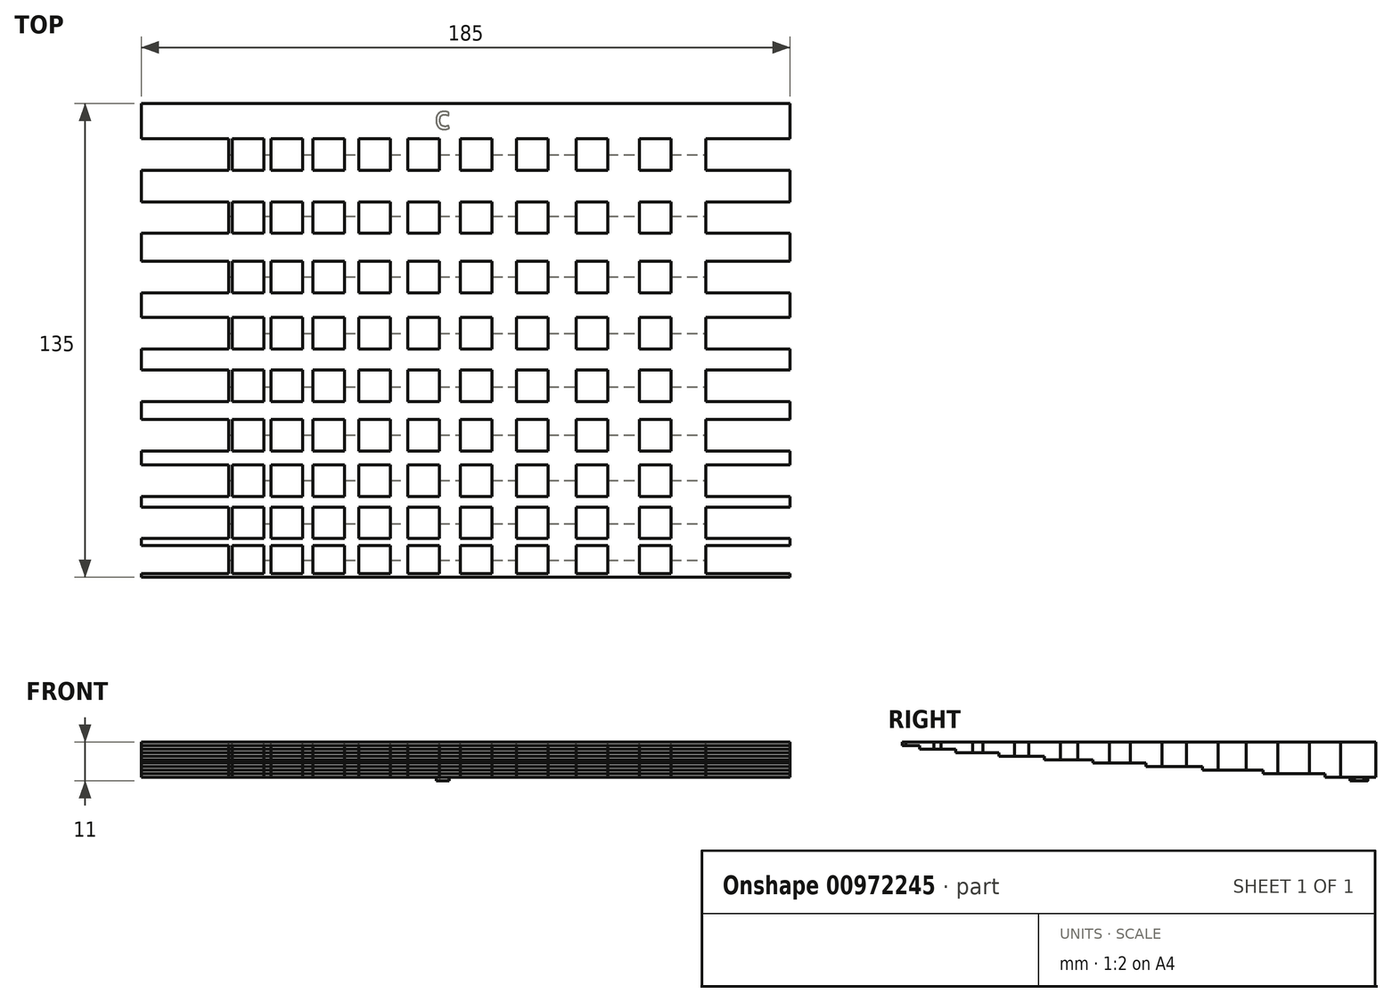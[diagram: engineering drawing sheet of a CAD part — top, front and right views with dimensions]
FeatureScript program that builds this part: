
annotation { "Feature Type Name" : "Feature", "Feature Type Description" : "" }
export const myFeature = defineFeature(function(context is Context, id is Id, definition is map)
    precondition{}
    {
        {
            var Q0;
            Q0=qCreatedBy(makeId("Top.planeOp"),FACE);
            var sketch = newSketch(context, id + "F0", { "sketchPlane" : qUnion([Q0])});
            skLineSegment(sketch, "E0.left", {"start": v(-99.72, 76) * mm, "end": v(-99.72, -59) * mm, "construction": true});
            skLineSegment(sketch, "E0.right", {"start": v(85.28, 76) * mm, "end": v(85.28, -59) * mm, "construction": true});
            skLineSegment(sketch, "E1.top", {"start": v(-99.72, 66) * mm, "end": v(85.28, 66) * mm});
            skLineSegment(sketch, "E1.left", {"start": v(-99.72, 76) * mm, "end": v(-99.72, 66) * mm});
            skLineSegment(sketch, "E1.right", {"start": v(85.28, 76) * mm, "end": v(85.28, 66) * mm});
            skLineSegment(sketch, "E2.left", {"start": v(-99.72, -58) * mm, "end": v(-99.72, -59) * mm});
            skLineSegment(sketch, "E2.right", {"start": v(85.28, -58) * mm, "end": v(85.28, -59) * mm});
            skLineSegment(sketch, "E3.bottom", {"start": v(-99.72, 57) * mm, "end": v(85.28, 57) * mm});
            skLineSegment(sketch, "E3.top", {"start": v(-99.72, 48) * mm, "end": v(85.28, 48) * mm});
            skLineSegment(sketch, "E3.left", {"start": v(-99.72, 57) * mm, "end": v(-99.72, 48) * mm});
            skLineSegment(sketch, "E3.right", {"start": v(85.28, 57) * mm, "end": v(85.28, 48) * mm});
            skLineSegment(sketch, "E4.bottom", {"start": v(-99.72, 39) * mm, "end": v(85.28, 39) * mm});
            skLineSegment(sketch, "E4.top", {"start": v(-99.72, 31) * mm, "end": v(85.28, 31) * mm});
            skLineSegment(sketch, "E4.left", {"start": v(-99.72, 39) * mm, "end": v(-99.72, 31) * mm});
            skLineSegment(sketch, "E4.right", {"start": v(85.28, 39) * mm, "end": v(85.28, 31) * mm});
            skLineSegment(sketch, "E5.bottom", {"start": v(-99.72, 22) * mm, "end": v(85.28, 22) * mm});
            skLineSegment(sketch, "E5.top", {"start": v(-99.72, 15) * mm, "end": v(85.28, 15) * mm});
            skLineSegment(sketch, "E5.left", {"start": v(-99.72, 22) * mm, "end": v(-99.72, 15) * mm});
            skLineSegment(sketch, "E5.right", {"start": v(85.28, 22) * mm, "end": v(85.28, 15) * mm});
            skLineSegment(sketch, "E6.bottom", {"start": v(-99.72, 6) * mm, "end": v(85.28, 6) * mm});
            skLineSegment(sketch, "E6.top", {"start": v(-99.72, 0) * mm, "end": v(85.28, 0) * mm});
            skLineSegment(sketch, "E6.left", {"start": v(-99.72, 6) * mm, "end": v(-99.72, 0) * mm});
            skLineSegment(sketch, "E6.right", {"start": v(85.28, 6) * mm, "end": v(85.28, 0) * mm});
            skLineSegment(sketch, "E7.bottom", {"start": v(-99.72, -9) * mm, "end": v(85.28, -9) * mm});
            skLineSegment(sketch, "E7.top", {"start": v(-99.72, -14) * mm, "end": v(85.28, -14) * mm});
            skLineSegment(sketch, "E7.left", {"start": v(-99.72, -9) * mm, "end": v(-99.72, -14) * mm});
            skLineSegment(sketch, "E7.right", {"start": v(85.28, -9) * mm, "end": v(85.28, -14) * mm});
            skLineSegment(sketch, "E8.bottom", {"start": v(-99.72, -23) * mm, "end": v(85.28, -23) * mm});
            skLineSegment(sketch, "E8.top", {"start": v(-99.72, -27) * mm, "end": v(85.28, -27) * mm});
            skLineSegment(sketch, "E8.left", {"start": v(-99.72, -23) * mm, "end": v(-99.72, -27) * mm});
            skLineSegment(sketch, "E8.right", {"start": v(85.28, -23) * mm, "end": v(85.28, -27) * mm});
            skLineSegment(sketch, "E9.bottom", {"start": v(-99.72, -36) * mm, "end": v(85.28, -36) * mm});
            skLineSegment(sketch, "E9.top", {"start": v(-99.72, -39) * mm, "end": v(85.28, -39) * mm});
            skLineSegment(sketch, "E9.left", {"start": v(-99.72, -36) * mm, "end": v(-99.72, -39) * mm});
            skLineSegment(sketch, "E9.right", {"start": v(85.28, -36) * mm, "end": v(85.28, -39) * mm});
            skLineSegment(sketch, "E10.bottom", {"start": v(-99.72, -48) * mm, "end": v(85.28, -48) * mm});
            skLineSegment(sketch, "E10.top", {"start": v(-99.72, -50) * mm, "end": v(85.28, -50) * mm});
            skLineSegment(sketch, "E10.left", {"start": v(-99.72, -48) * mm, "end": v(-99.72, -50) * mm});
            skLineSegment(sketch, "E10.right", {"start": v(85.28, -48) * mm, "end": v(85.28, -50) * mm});
            skLineSegment(sketch, "E11", {"start": v(-99.72, 76) * mm, "end": v(85.28, 76) * mm});
            skLineSegment(sketch, "E12", {"start": v(-99.72, -59) * mm, "end": v(85.28, -59) * mm});
            skLineSegment(sketch, "E13", {"start": v(85.28, -58) * mm, "end": v(-99.72, -58) * mm});
            skSolve(sketch);
        }
        {
            var Q0;
            Q0=qCreatedBy(makeId("Top.planeOp"),FACE);
            var sketch = newSketch(context, id + "F1", { "sketchPlane" : qUnion([Q0])});
            skLineSegment(sketch, "E14.0", {"start": v(-99.72, 76) * mm, "end": v(85.28, 76) * mm, "construction": true});
            skLineSegment(sketch, "E15.0", {"start": v(-99.72, -59) * mm, "end": v(85.28, -59) * mm, "construction": true});
            skLineSegment(sketch, "E16.bottom", {"start": v(61.28, 76) * mm, "end": v(51.28, 76) * mm});
            skLineSegment(sketch, "E16.top", {"start": v(61.28, -59) * mm, "end": v(51.28, -59) * mm});
            skLineSegment(sketch, "E16.left", {"start": v(61.28, 76) * mm, "end": v(61.28, -59) * mm});
            skLineSegment(sketch, "E16.right", {"start": v(51.28, 76) * mm, "end": v(51.28, -59) * mm});
            skLineSegment(sketch, "E17.bottom", {"start": v(42.28, 76) * mm, "end": v(33.28, 76) * mm});
            skLineSegment(sketch, "E17.top", {"start": v(42.28, -59) * mm, "end": v(33.28, -59) * mm});
            skLineSegment(sketch, "E17.left", {"start": v(42.28, 76) * mm, "end": v(42.28, -59) * mm});
            skLineSegment(sketch, "E17.right", {"start": v(33.28, 76) * mm, "end": v(33.28, -59) * mm});
            skLineSegment(sketch, "E18.bottom", {"start": v(24.28, 76) * mm, "end": v(16.28, 76) * mm});
            skLineSegment(sketch, "E18.top", {"start": v(24.28, -59) * mm, "end": v(16.28, -59) * mm});
            skLineSegment(sketch, "E18.left", {"start": v(24.28, 76) * mm, "end": v(24.28, -59) * mm});
            skLineSegment(sketch, "E18.right", {"start": v(16.28, 76) * mm, "end": v(16.28, -59) * mm});
            skLineSegment(sketch, "E19.bottom", {"start": v(7.28, 76) * mm, "end": v(0.28, 76) * mm});
            skLineSegment(sketch, "E19.top", {"start": v(7.28, -59) * mm, "end": v(0.28, -59) * mm});
            skLineSegment(sketch, "E19.left", {"start": v(7.28, 76) * mm, "end": v(7.28, -59) * mm});
            skLineSegment(sketch, "E19.right", {"start": v(0.28, 76) * mm, "end": v(0.28, -59) * mm});
            skLineSegment(sketch, "E20.bottom", {"start": v(-8.72, 76) * mm, "end": v(-14.72, 76) * mm});
            skLineSegment(sketch, "E20.top", {"start": v(-8.72, -59) * mm, "end": v(-14.72, -59) * mm});
            skLineSegment(sketch, "E20.left", {"start": v(-8.72, 76) * mm, "end": v(-8.72, -59) * mm});
            skLineSegment(sketch, "E20.right", {"start": v(-14.72, 76) * mm, "end": v(-14.72, -59) * mm});
            skLineSegment(sketch, "E21.bottom", {"start": v(-23.72, 76) * mm, "end": v(-28.72, 76) * mm});
            skLineSegment(sketch, "E21.top", {"start": v(-23.72, -59) * mm, "end": v(-28.72, -59) * mm});
            skLineSegment(sketch, "E21.left", {"start": v(-23.72, 76) * mm, "end": v(-23.72, -59) * mm});
            skLineSegment(sketch, "E21.right", {"start": v(-28.72, 76) * mm, "end": v(-28.72, -59) * mm});
            skLineSegment(sketch, "E22.bottom", {"start": v(-37.72, 76) * mm, "end": v(-41.72, 76) * mm});
            skLineSegment(sketch, "E22.top", {"start": v(-37.72, -59) * mm, "end": v(-41.72, -59) * mm});
            skLineSegment(sketch, "E22.left", {"start": v(-37.72, 76) * mm, "end": v(-37.72, -59) * mm});
            skLineSegment(sketch, "E22.right", {"start": v(-41.72, 76) * mm, "end": v(-41.72, -59) * mm});
            skLineSegment(sketch, "E23.bottom", {"start": v(-50.72, 76) * mm, "end": v(-53.72, 76) * mm});
            skLineSegment(sketch, "E23.top", {"start": v(-50.72, -59) * mm, "end": v(-53.72, -59) * mm});
            skLineSegment(sketch, "E23.left", {"start": v(-50.72, 76) * mm, "end": v(-50.72, -59) * mm});
            skLineSegment(sketch, "E23.right", {"start": v(-53.72, 76) * mm, "end": v(-53.72, -59) * mm});
            skLineSegment(sketch, "E24.bottom", {"start": v(-62.72, 76) * mm, "end": v(-64.72, 76) * mm});
            skLineSegment(sketch, "E24.top", {"start": v(-62.72, -59) * mm, "end": v(-64.72, -59) * mm});
            skLineSegment(sketch, "E24.left", {"start": v(-62.72, 76) * mm, "end": v(-62.72, -59) * mm});
            skLineSegment(sketch, "E24.right", {"start": v(-64.72, 76) * mm, "end": v(-64.72, -59) * mm});
            skLineSegment(sketch, "E25.bottom", {"start": v(-73.72, 76) * mm, "end": v(-74.72, 76) * mm});
            skLineSegment(sketch, "E25.top", {"start": v(-73.72, -59) * mm, "end": v(-74.72, -59) * mm});
            skLineSegment(sketch, "E25.left", {"start": v(-73.72, 76) * mm, "end": v(-73.72, -59) * mm});
            skLineSegment(sketch, "E25.right", {"start": v(-74.72, 76) * mm, "end": v(-74.72, -59) * mm});
            skSolve(sketch);
        }
        {
            var Q0;
            Q0 = qSketchRegion(id + "F0", true);
            extrude(context, id + "F2", {"entities" : qUnion([Q0]), "depth" : 10 * mm, "offsetDistance" : 25 * mm});
        }
        {
            var Q0;
            Q0 = qSketchRegion(id + "F1", true);
            extrude(context, id + "F3", {"entities" : qUnion([Q0]), "operationType" : NewBodyOperationType.ADD, "depth" : 10 * mm, "offsetDistance" : 25 * mm});
        }
        {
            var Q0;
            Q0=qCreatedBy(makeId("Right.planeOp"),FACE);
            cPlane(context, id + "F4", {"entities" : qUnion([Q0]), "cplaneType" : CPlaneType.OFFSET, "offset" : 100 * mm, "width" : 150 * mm, "height" : 150 * mm});
        }
        {
            var Q0;
            Q0=qCreatedBy(id+"F4.planeOp",FACE);
            var sketch = newSketch(context, id + "F5", { "sketchPlane" : qUnion([Q0])});
            skLineSegment(sketch, "E26", {"start": v(61.44, 0) * mm, "end": v(-63.86, 0) * mm});
            skLineSegment(sketch, "E27", {"start": v(-63.86, 0) * mm, "end": v(-63.86, 9) * mm});
            skLineSegment(sketch, "E28", {"start": v(-63.86, 9) * mm, "end": v(-54.11, 9) * mm});
            skLineSegment(sketch, "E29", {"start": v(-54.11, 9) * mm, "end": v(-54.11, 8) * mm});
            skLineSegment(sketch, "E30", {"start": v(-54.11, 8) * mm, "end": v(-43.8, 8) * mm});
            skLineSegment(sketch, "E31", {"start": v(-43.8, 8) * mm, "end": v(-43.8, 7) * mm});
            skLineSegment(sketch, "E32", {"start": v(-43.8, 7) * mm, "end": v(-31.43, 7) * mm});
            skLineSegment(sketch, "E33", {"start": v(-31.43, 7) * mm, "end": v(-31.43, 6) * mm});
            skLineSegment(sketch, "E34", {"start": v(-31.43, 6) * mm, "end": v(-18.46, 6) * mm});
            skLineSegment(sketch, "E35", {"start": v(-18.46, 6) * mm, "end": v(-18.46, 5) * mm});
            skLineSegment(sketch, "E36", {"start": v(-18.46, 5) * mm, "end": v(-4.73, 5) * mm});
            skLineSegment(sketch, "E37", {"start": v(-4.73, 5) * mm, "end": v(-4.73, 4) * mm});
            skLineSegment(sketch, "E38", {"start": v(-4.73, 4) * mm, "end": v(10.45, 4) * mm});
            skLineSegment(sketch, "E39", {"start": v(10.45, 4) * mm, "end": v(10.45, 3) * mm});
            skLineSegment(sketch, "E40", {"start": v(10.45, 3) * mm, "end": v(26.55, 3) * mm});
            skLineSegment(sketch, "E41", {"start": v(26.55, 3) * mm, "end": v(26.55, 2) * mm});
            skLineSegment(sketch, "E42", {"start": v(26.55, 2) * mm, "end": v(43.86, 2) * mm});
            skLineSegment(sketch, "E43", {"start": v(43.86, 2) * mm, "end": v(43.86, 1) * mm});
            skLineSegment(sketch, "E44", {"start": v(43.86, 1) * mm, "end": v(61.44, 1) * mm});
            skLineSegment(sketch, "E45", {"start": v(61.44, 1) * mm, "end": v(61.44, 0) * mm});
            skPoint(sketch, "E46.orphan", {"position": v(80.66, 0) * mm});
            skSolve(sketch);
        }
        {
            var Q0;
            Q0 = qSketchRegion(id + "F5", true);
            extrude(context, id + "F6", {"entities" : qUnion([Q0]), "operationType" : NewBodyOperationType.REMOVE, "endBound" : BoundingType.THROUGH_ALL, "oppositeDirection" : true, "depth" : 25 * mm, "offsetDistance" : 25 * mm});
        }
        {
            var Q0;
            Q0=makeQuery(id+"F3.boolean.opBoolean","MERGE",FACE,{"derivedFrom":[makeQuery(id+"F2.opExtrude","CAP_FACE",FACE,{"disambiguationData":[OSD([sQuery(id+"F0.wireOp",EDGE,"E1.top"),sQuery(id+"F0.wireOp",EDGE,"E1.left"),sQuery(id+"F0.wireOp",EDGE,"E1.right"),sQuery(id+"F0.wireOp",EDGE,"E11")])],"isStart":true}),makeQuery(id+"F2.opExtrude","CAP_FACE",FACE,{"disambiguationData":[OSD([sQuery(id+"F0.wireOp",EDGE,"E2.left"),sQuery(id+"F0.wireOp",EDGE,"E2.right"),sQuery(id+"F0.wireOp",EDGE,"E12"),sQuery(id+"F0.wireOp",EDGE,"E13")])],"isStart":true}),makeQuery(id+"F2.opExtrude","CAP_FACE",FACE,{"disambiguationData":[OSD([sQuery(id+"F0.wireOp",EDGE,"E3.bottom"),sQuery(id+"F0.wireOp",EDGE,"E3.top"),sQuery(id+"F0.wireOp",EDGE,"E3.left"),sQuery(id+"F0.wireOp",EDGE,"E3.right")])],"isStart":true}),makeQuery(id+"F2.opExtrude","CAP_FACE",FACE,{"disambiguationData":[OSD([sQuery(id+"F0.wireOp",EDGE,"E4.bottom"),sQuery(id+"F0.wireOp",EDGE,"E4.top"),sQuery(id+"F0.wireOp",EDGE,"E4.left"),sQuery(id+"F0.wireOp",EDGE,"E4.right")])],"isStart":true}),makeQuery(id+"F2.opExtrude","CAP_FACE",FACE,{"disambiguationData":[OSD([sQuery(id+"F0.wireOp",EDGE,"E5.bottom"),sQuery(id+"F0.wireOp",EDGE,"E5.top"),sQuery(id+"F0.wireOp",EDGE,"E5.left"),sQuery(id+"F0.wireOp",EDGE,"E5.right")])],"isStart":true}),makeQuery(id+"F2.opExtrude","CAP_FACE",FACE,{"disambiguationData":[OSD([sQuery(id+"F0.wireOp",EDGE,"E6.bottom"),sQuery(id+"F0.wireOp",EDGE,"E6.top"),sQuery(id+"F0.wireOp",EDGE,"E6.left"),sQuery(id+"F0.wireOp",EDGE,"E6.right")])],"isStart":true}),makeQuery(id+"F2.opExtrude","CAP_FACE",FACE,{"disambiguationData":[OSD([sQuery(id+"F0.wireOp",EDGE,"E7.bottom"),sQuery(id+"F0.wireOp",EDGE,"E7.top"),sQuery(id+"F0.wireOp",EDGE,"E7.left"),sQuery(id+"F0.wireOp",EDGE,"E7.right")])],"isStart":true}),makeQuery(id+"F2.opExtrude","CAP_FACE",FACE,{"disambiguationData":[OSD([sQuery(id+"F0.wireOp",EDGE,"E8.bottom"),sQuery(id+"F0.wireOp",EDGE,"E8.top"),sQuery(id+"F0.wireOp",EDGE,"E8.left"),sQuery(id+"F0.wireOp",EDGE,"E8.right")])],"isStart":true}),makeQuery(id+"F2.opExtrude","CAP_FACE",FACE,{"disambiguationData":[OSD([sQuery(id+"F0.wireOp",EDGE,"E9.bottom"),sQuery(id+"F0.wireOp",EDGE,"E9.top"),sQuery(id+"F0.wireOp",EDGE,"E9.left"),sQuery(id+"F0.wireOp",EDGE,"E9.right")])],"isStart":true}),makeQuery(id+"F2.opExtrude","CAP_FACE",FACE,{"disambiguationData":[OSD([sQuery(id+"F0.wireOp",EDGE,"E10.bottom"),sQuery(id+"F0.wireOp",EDGE,"E10.top"),sQuery(id+"F0.wireOp",EDGE,"E10.left"),sQuery(id+"F0.wireOp",EDGE,"E10.right")])],"isStart":true}),makeQuery(id+"F3.opExtrude","CAP_FACE",FACE,{"disambiguationData":[OSD([sQuery(id+"F1.wireOp",EDGE,"E16.bottom"),sQuery(id+"F1.wireOp",EDGE,"E16.top"),sQuery(id+"F1.wireOp",EDGE,"E16.left"),sQuery(id+"F1.wireOp",EDGE,"E16.right")])],"isStart":true}),makeQuery(id+"F3.opExtrude","CAP_FACE",FACE,{"disambiguationData":[OSD([sQuery(id+"F1.wireOp",EDGE,"E17.bottom"),sQuery(id+"F1.wireOp",EDGE,"E17.top"),sQuery(id+"F1.wireOp",EDGE,"E17.left"),sQuery(id+"F1.wireOp",EDGE,"E17.right")])],"isStart":true}),makeQuery(id+"F3.opExtrude","CAP_FACE",FACE,{"disambiguationData":[OSD([sQuery(id+"F1.wireOp",EDGE,"E18.bottom"),sQuery(id+"F1.wireOp",EDGE,"E18.top"),sQuery(id+"F1.wireOp",EDGE,"E18.left"),sQuery(id+"F1.wireOp",EDGE,"E18.right")])],"isStart":true}),makeQuery(id+"F3.opExtrude","CAP_FACE",FACE,{"disambiguationData":[OSD([sQuery(id+"F1.wireOp",EDGE,"E19.bottom"),sQuery(id+"F1.wireOp",EDGE,"E19.top"),sQuery(id+"F1.wireOp",EDGE,"E19.left"),sQuery(id+"F1.wireOp",EDGE,"E19.right")])],"isStart":true}),makeQuery(id+"F3.opExtrude","CAP_FACE",FACE,{"disambiguationData":[OSD([sQuery(id+"F1.wireOp",EDGE,"E20.bottom"),sQuery(id+"F1.wireOp",EDGE,"E20.top"),sQuery(id+"F1.wireOp",EDGE,"E20.left"),sQuery(id+"F1.wireOp",EDGE,"E20.right")])],"isStart":true}),makeQuery(id+"F3.opExtrude","CAP_FACE",FACE,{"disambiguationData":[OSD([sQuery(id+"F1.wireOp",EDGE,"E21.bottom"),sQuery(id+"F1.wireOp",EDGE,"E21.top"),sQuery(id+"F1.wireOp",EDGE,"E21.left"),sQuery(id+"F1.wireOp",EDGE,"E21.right")])],"isStart":true}),makeQuery(id+"F3.opExtrude","CAP_FACE",FACE,{"disambiguationData":[OSD([sQuery(id+"F1.wireOp",EDGE,"E22.bottom"),sQuery(id+"F1.wireOp",EDGE,"E22.top"),sQuery(id+"F1.wireOp",EDGE,"E22.left"),sQuery(id+"F1.wireOp",EDGE,"E22.right")])],"isStart":true}),makeQuery(id+"F3.opExtrude","CAP_FACE",FACE,{"disambiguationData":[OSD([sQuery(id+"F1.wireOp",EDGE,"E23.bottom"),sQuery(id+"F1.wireOp",EDGE,"E23.top"),sQuery(id+"F1.wireOp",EDGE,"E23.left"),sQuery(id+"F1.wireOp",EDGE,"E23.right")])],"isStart":true}),makeQuery(id+"F3.opExtrude","CAP_FACE",FACE,{"disambiguationData":[OSD([sQuery(id+"F1.wireOp",EDGE,"E24.bottom"),sQuery(id+"F1.wireOp",EDGE,"E24.top"),sQuery(id+"F1.wireOp",EDGE,"E24.left"),sQuery(id+"F1.wireOp",EDGE,"E24.right")])],"isStart":true}),makeQuery(id+"F3.opExtrude","CAP_FACE",FACE,{"disambiguationData":[OSD([sQuery(id+"F1.wireOp",EDGE,"E25.bottom"),sQuery(id+"F1.wireOp",EDGE,"E25.top"),sQuery(id+"F1.wireOp",EDGE,"E25.left"),sQuery(id+"F1.wireOp",EDGE,"E25.right")])],"isStart":true})]});
            var sketch = newSketch(context, id + "F7", { "sketchPlane" : qUnion([Q0])});
            skText(sketch, "E47", { "text": "C", "fontName": "OpenSans-Bold.ttf"});
            const initialGuessF7  = {"E47": [-0.01604, -0.07365, 1, 0, 0.005]};
            skSetInitialGuess(sketch, initialGuessF7);
            skSolve(sketch);
        }
        {
            var Q0;
            Q0 = qSketchRegion(id + "F7", true);
            extrude(context, id + "F8", {"entities" : qUnion([Q0]), "operationType" : NewBodyOperationType.ADD, "depth" : 1 * mm, "offsetDistance" : 25 * mm});
        }
    });
